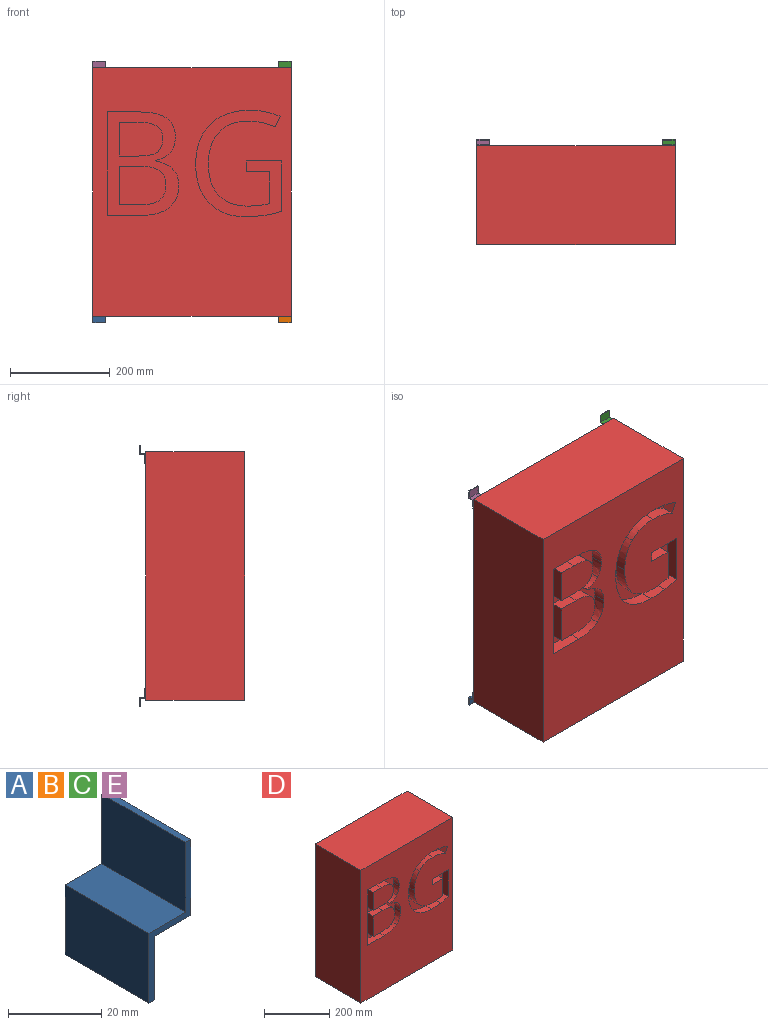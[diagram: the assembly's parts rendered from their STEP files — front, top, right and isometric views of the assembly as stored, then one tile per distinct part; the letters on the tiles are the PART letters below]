
ASSEMBLY  parts=5 mates=4
PART A: 10 faces, bbox 12.7x25.4x36.5 mm
  f0: plane 25.4x1.59mm, normal (0,0,1), area 40.3mm2, adj f1,f7,f8,f9
  f1: plane 25.4x18.26mm, normal (-1,0,0), area 463.7mm2, adj f0,f2,f8,f9
  f2: plane 25.4x11.11mm, normal (0,0,1), area 282.3mm2, adj f1,f3,f8,f9
  f3: plane 25.4x18.26mm, normal (-1,0,0), area 463.7mm2, adj f2,f4,f8,f9
  f4: plane 25.4x1.59mm, normal (0,0,-1), area 40.3mm2, adj f3,f5,f8,f9
  f5: plane 25.4x16.67mm, normal (1,0,0), area 423.4mm2, adj f4,f6,f8,f9
  f6: plane 25.4x11.11mm, normal (0,0,-1), area 282.3mm2, adj f5,f7,f8,f9
  f7: plane 25.4x19.84mm, normal (1,0,0), area 504mm2, adj f0,f6,f8,f9
  f8: plane 36.51x12.7mm, normal (0,-1,0), area 75.6mm2, adj f0,f1,f2,f3,f4,f5,f6,f7
  f9: plane 36.51x12.7mm, normal (0,1,0), area 75.6mm2, adj f0,f1,f2,f3,f4,f5,f6,f7
PART B: same geometry as A
PART C: same geometry as A
PART D: 55 faces, bbox 398.5x198.4x498.5 mm
  f0: plane 498.48x398.46mm, normal (0,-1,0), area 158631.4mm2, adj f1,f2,f3,f4,f18,f19,f20,f21
  f1: plane 498.48x198.44mm, normal (-1,0,0), area 98916.1mm2, adj f0,f2,f4,f5
  f2: plane 398.46x198.44mm, normal (0,0,-1), area 79069.9mm2, adj f0,f1,f3,f5
  f3: plane 498.48x198.44mm, normal (1,0,0), area 98916.1mm2, adj f0,f2,f4,f5
  f4: plane 398.46x198.44mm, normal (0,0,1), area 79069.9mm2, adj f0,f1,f3,f5
  f5: plane 498.48x398.46mm, normal (0,1,0), area 198623.6mm2, adj f1,f2,f3,f4
  f6: plane 77.84x25.4mm, normal (-1,0,0), area 1977.2mm2, adj f7,f30,f31,f54
  f7: plane 41.43x25.4mm, normal (0,0,1), area 1052.2mm2, adj f6,f8,f31,f54
  f8: extruded ~39.61x25.4mm, area 1047.4mm2, adj f7,f9,f31,f54
  f9: extruded ~28.45x25.4mm, area 828.8mm2, adj f8,f10,f31,f54
  f10: extruded ~30.55x25.4mm, area 872.6mm2, adj f9,f11,f31,f54
  f11: extruded ~37.9x25.4mm, area 1011.2mm2, adj f10,f30,f31,f54
  f12: plane 39.83x25.4mm, normal (0,0,-1), area 1011.7mm2, adj f13,f28,f31,f32
  f13: plane 68.1x25.4mm, normal (-1,0,0), area 1729.8mm2, adj f12,f14,f31,f32
  f14: plane 35.6x25.4mm, normal (0,0,1), area 904.2mm2, adj f13,f15,f31,f32
  f15: extruded ~39.83x25.4mm, area 1042.6mm2, adj f14,f16,f31,f32
  f16: extruded ~25.4x25.27mm, area 751.3mm2, adj f15,f17,f31,f32
  f17: extruded ~27.06x25.4mm, area 774.7mm2, adj f16,f28,f31,f32
  f18: plane 58.77x25.4mm, normal (0,0,-1), area 1492.8mm2, adj f0,f19,f29,f31
  f19: plane 207.99x25.4mm, normal (1,0,0), area 5283.1mm2, adj f0,f18,f20,f31
  f20: plane 72.56x25.4mm, normal (0,0,1), area 1843.1mm2, adj f0,f19,f21,f31
  f21: extruded ~52.72x25.4mm, area 1425.4mm2, adj f0,f20,f22,f31
  f22: extruded ~43.52x25.4mm, area 1247.2mm2, adj f0,f21,f23,f31
  f23: extruded ~49.8x47.39mm, area 1933.3mm2, adj f0,f22,f24,f31
  f24: plane 25.4x1.41mm, normal (-1,0,0), area 35.8mm2, adj f0,f23,f25,f31
  f25: extruded ~30.11x25.4mm, area 878.5mm2, adj f0,f24,f26,f31
  f26: extruded ~30.55x25.4mm, area 837mm2, adj f0,f25,f27,f31
  f27: extruded ~39.1x25.4mm, area 1148.4mm2, adj f0,f26,f29,f31
  f28: extruded ~36.87x25.4mm, area 972.6mm2, adj f12,f17,f31,f32
  f29: extruded ~59.89x25.4mm, area 1573.7mm2, adj f0,f18,f27,f31
  f30: plane 43.43x25.4mm, normal (0,0,-1), area 1103.1mm2, adj f6,f11,f31,f54
  f31: plane 207.99x144.13mm, normal (0,-1,0), area 14753.1mm2, adj f6,f7,f8,f9,f10,f11,f12,f13
  f32: plane 87.95x68.1mm, normal (0,-1,0), area 5473.4mm2, adj f12,f13,f14,f15,f16,f17,f28
  f33: plane 70.7x25.4mm, normal (0,0,-1), area 1795.7mm2, adj f0,f34,f52,f53
  f34: plane 25.4x21.62mm, normal (1,0,0), area 549.2mm2, adj f0,f33,f35,f53
  f35: plane 46.48x25.4mm, normal (0,0,1), area 1180.6mm2, adj f0,f34,f36,f53
  f36: plane 64.01x25.4mm, normal (1,0,0), area 1625.7mm2, adj f0,f35,f37,f53
  f37: extruded ~42.25x25.4mm, area 1083.1mm2, adj f0,f36,f38,f53
  f38: extruded ~60.39x25.4mm, area 1677.9mm2, adj f0,f37,f39,f53
  f39: extruded ~63.87x25.4mm, area 1746.2mm2, adj f0,f38,f40,f53
  f40: extruded ~62.75x25.4mm, area 1725.9mm2, adj f0,f39,f41,f53
  f41: extruded ~59.32x25.4mm, area 1660.2mm2, adj f0,f40,f42,f53
  f42: extruded ~54.22x25.4mm, area 1419.6mm2, adj f0,f41,f43,f53
  f43: plane 25.4x21.35mm, normal (-0.92,0,0.4), area 592.3mm2, adj f0,f42,f44,f53
  f44: extruded ~62.05x25.4mm, area 1617.2mm2, adj f0,f43,f45,f53
  f45: extruded ~57.29x25.4mm, area 1506.2mm2, adj f0,f44,f46,f53
  f46: extruded ~37.49x37.26mm, area 1363.4mm2, adj f0,f45,f47,f53
  f47: extruded ~56.86x25.4mm, area 1496.7mm2, adj f0,f46,f48,f53
  f48: extruded ~78.73x26.31mm, area 2160.6mm2, adj f0,f47,f49,f53
  f49: extruded ~73.52x28.11mm, area 2059.3mm2, adj f0,f48,f50,f53
  f50: extruded ~39.56x25.4mm, area 1008.2mm2, adj f0,f49,f51,f53
  f51: extruded ~33.6x25.4mm, area 878mm2, adj f0,f50,f52,f53
  f52: plane 101.15x25.4mm, normal (-1,0,0), area 2569.3mm2, adj f0,f33,f51,f53
  f53: plane 213.82x172.99mm, normal (0,-1,0), area 13096.7mm2, adj f33,f34,f35,f36,f37,f38,f39,f40
  f54: plane 94.05x77.84mm, normal (0,-1,0), area 6669mm2, adj f6,f7,f8,f9,f10,f11,f30
PART E: same geometry as A
PLACE A rot(axis=(0,0,-1),90deg) t=(-173.83,-26.99,-13.89)mm
PLACE B rot(axis=(0,0,-1),90deg) t=(199.23,-26.99,-13.89)mm
PLACE C rot(axis=(0.71,-0.71,0),180deg) t=(173.83,-26.99,512.37)mm
PLACE D t=(-199.23,0,0)mm
PLACE E rot(axis=(0.71,-0.71,0),180deg) t=(-199.23,-26.99,512.37)mm
MATE fastened A.f7 <-> D.f5  axis (0,-1,0) through (-186.53,0,12.7)mm
MATE fastened C.f7 <-> D.f5  axis (0,-1,0) through (186.53,0,485.78)mm
MATE fastened D.f5 <-> E.f7  axis (0,1,0) through (-199.23,0,498.48)mm
MATE fastened D.f5 <-> B.f7  axis (0,1,0) through (199.23,0,0)mm
